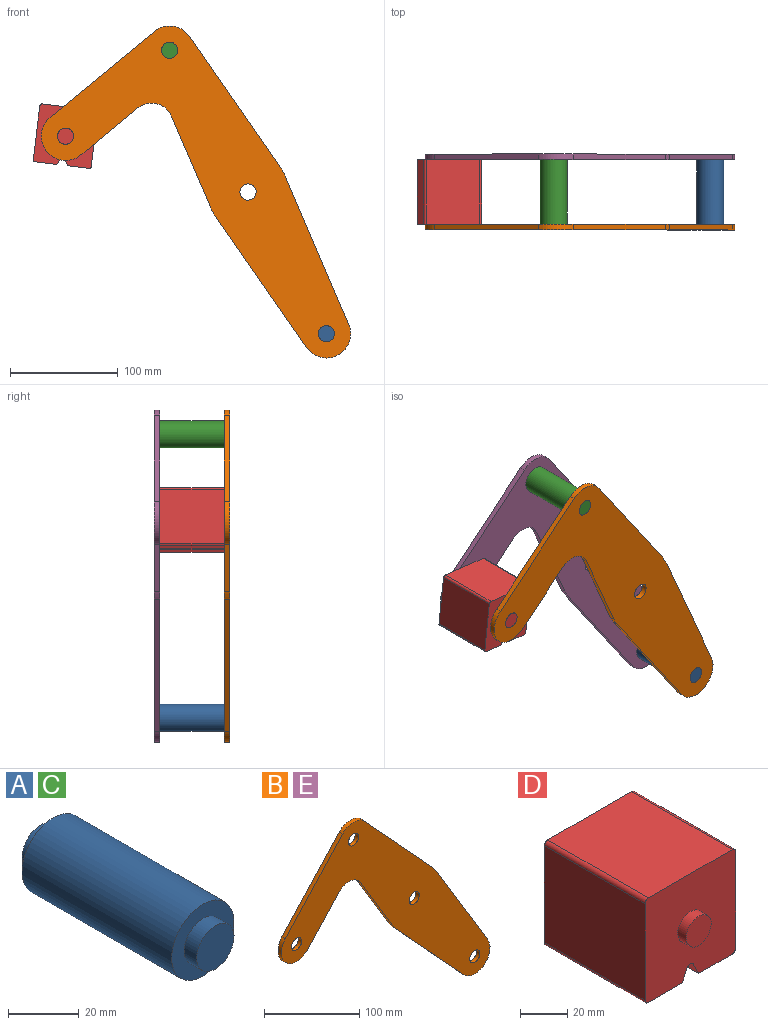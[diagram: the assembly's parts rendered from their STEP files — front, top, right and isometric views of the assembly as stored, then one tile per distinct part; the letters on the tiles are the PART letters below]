
ASSEMBLY  parts=5 mates=3
PART A: 7 faces, bbox 25x70x25 mm
  f0: cylinder r=12.5mm len=60mm, axis (0,-1,0), area 4712.4mm2, adj f2,f5
  f1: cylinder r=7.5mm len=15mm, axis (0,1,0), area 235.6mm2, adj f2,f3
  f2: plane 25x25mm, normal (0,-1,0), area 314.2mm2, adj f0,f1
  f3: plane 15x15mm, normal (0,-1,0), area 176.7mm2, adj f1
  f4: cylinder r=7.5mm len=15mm, axis (0,-1,0), area 235.6mm2, adj f5,f6
  f5: plane 25x25mm, normal (0,1,0), area 314.2mm2, adj f0,f4
  f6: plane 15x15mm, normal (0,1,0), area 176.7mm2, adj f4
PART B: 18 faces, bbox 309.5x5x285.1 mm
  f0: cylinder r=22.5mm len=39.07mm, axis (0,1,0), area 353.4mm2, adj f1,f13,f16,f17
  f1: plane 50.28x46.21mm, normal (0.74,0,-0.68), area 341.4mm2, adj f0,f2,f16,f17
  f2: cylinder r=20mm len=31.85mm, axis (0,1,0), area 185.5mm2, adj f1,f3,f16,f17
  f3: plane 79.23x47.81mm, normal (-0.86,0,-0.52), area 462.7mm2, adj f2,f4,f16,f17
  f4: cylinder r=37.5mm len=6mm, axis (0,1,0), area 37.6mm2, adj f3,f5,f16,f17
  f5: plane 109.88x101mm, normal (-0.74,0,-0.68), area 746.2mm2, adj f4,f6,f16,f17
  f6: cylinder r=22.5mm len=39.07mm, axis (0,1,0), area 330.9mm2, adj f5,f7,f16,f17
  f7: plane 127.78x77.11mm, normal (0.86,0,0.52), area 746.2mm2, adj f6,f8,f16,f17
  f8: cylinder r=37.5mm len=6mm, axis (0,1,0), area 37.6mm2, adj f7,f9,f16,f17
  f9: plane 109.88x101mm, normal (0.74,0,0.68), area 746.2mm2, adj f8,f10,f16,f17
  f10: cylinder r=22.5mm len=33.13mm, axis (0,1,0), area 186.2mm2, adj f9,f13,f16,f17
  f11: cylinder r=7.5mm len=15mm, axis (0,1,0), area 235.6mm2, adj f16,f17
  f12: cylinder r=7.5mm len=15mm, axis (0,1,0), area 235.6mm2, adj f16,f17
  f13: plane 92.03x84.59mm, normal (-0.74,0,0.68), area 625mm2, adj f0,f10,f16,f17
  f14: cylinder r=7.5mm len=15mm, axis (0,1,0), area 235.6mm2, adj f16,f17
  f15: cylinder r=7.5mm len=15mm, axis (0,1,0), area 235.6mm2, adj f16,f17
  f16: plane 309.5x285.07mm, normal (0,-1,0), area 24555.4mm2, adj f0,f1,f2,f3,f4,f5,f6,f7
  f17: plane 309.5x285.07mm, normal (0,1,0), area 24555.4mm2, adj f0,f1,f2,f3,f4,f5,f6,f7
PART C: same geometry as A
PART D: 18 faces, bbox 54x70x54 mm
  f0: plane 60x50.01mm, normal (0,0,1), area 3000.4mm2, adj f4,f10,f13,f14
  f1: plane 60x50.01mm, normal (-1,0,0), area 3000.4mm2, adj f4,f10,f14,f15
  f2: plane 60x20mm, normal (0,0,-1), area 1200.2mm2, adj f3,f4,f10,f15
  f3: plane 60x6.42mm, normal (0.89,0,-0.45), area 430.8mm2, adj f2,f4,f10,f16
  f4: plane 54.01x54.01mm, normal (0,-1,0), area 2690.1mm2, adj f0,f1,f2,f3,f5,f6,f7,f9
  f5: plane 60x50.01mm, normal (1,0,0), area 3000.4mm2, adj f4,f10,f13,f17
  f6: plane 60x6.42mm, normal (-0.89,0,-0.45), area 430.8mm2, adj f4,f7,f10,f16
  f7: plane 60x20mm, normal (0,0,-1), area 1200.2mm2, adj f4,f6,f10,f17
  f8: plane 15x15mm, normal (0,-1,0), area 176.7mm2, adj f9
  f9: cylinder r=7.5mm len=15mm, axis (0,1,0), area 235.6mm2, adj f4,f8
  f10: plane 54.01x54.01mm, normal (0,1,0), area 2690.1mm2, adj f0,f1,f2,f3,f5,f6,f7,f12
  f11: plane 15x15mm, normal (0,1,0), area 176.7mm2, adj f12
  f12: cylinder r=7.5mm len=15mm, axis (0,-1,0), area 235.6mm2, adj f10,f11
  f13: cylinder r=2mm len=60mm, axis (0,-1,0), area 188.5mm2, adj f0,f4,f5,f10
  f14: cylinder r=2mm len=60mm, axis (0,1,0), area 188.5mm2, adj f0,f1,f4,f10
  f15: cylinder r=2mm len=60mm, axis (0,-1,0), area 188.5mm2, adj f1,f2,f4,f10
  f16: cylinder r=2mm len=60mm, axis (0,-1,0), area 265.7mm2, adj f3,f4,f6,f10
  f17: cylinder r=2mm len=60mm, axis (0,1,0), area 188.5mm2, adj f4,f5,f7,f10
PART E: same geometry as B
PLACE A rot(axis=(0,1,0),7.9deg) t=(145.21,-30,-262.52)mm
PLACE B rot(axis=(0,1,0),7.9deg) t=(0,-30,0)mm fixed
PLACE C rot(axis=(0,1,0),7.9deg) t=(0,-30,0)mm
PLACE D rot(axis=(0,1,0),6.9deg) t=(0.92,-30,3.11)mm
PLACE E rot(axis=(0,1,0),7.9deg) t=(0,35,0)mm
MATE fastened C.f0 <-> E.f10  axis (0,1,0) through (-72.6,30,131.26)mm
MATE revolute B.f0 <-> D.f9  axis (0,1,0) through (-169.04,-30,51.73)mm
MATE fastened B.f6 <-> A.f0  axis (0,1,0) through (72.6,-30,-131.26)mm
